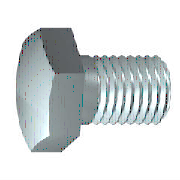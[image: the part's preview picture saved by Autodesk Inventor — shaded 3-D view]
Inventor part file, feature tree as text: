
AUTODESK INVENTOR PART (.ipt)
format: ipt  version: 2025.2 (Build 292293000, 293)  size: 201,216 bytes
history: native  units: mm (DEFAULTED — no unit token found)
features: other x6, plane x3, chamfer x1
ambient origin geometry x6: Origin, XY Plane, X Axis, Y Axis, Z Axis, Center Point
bodies: Solid1 (feature_tree)
feature tree (10):
  plane  "WorkPlane1"
  other  "WorkPoint1"
  other  "Drehung1"
  other  "Drehung2"
  chamfer  "Fase1"  Distance=30.0mm
  other  "MSC_A1"
  other  "MSC_PF1"
  other  "MSC_PT1"
  plane  "WorkPlane2"
  plane  "WorkPlane3"
